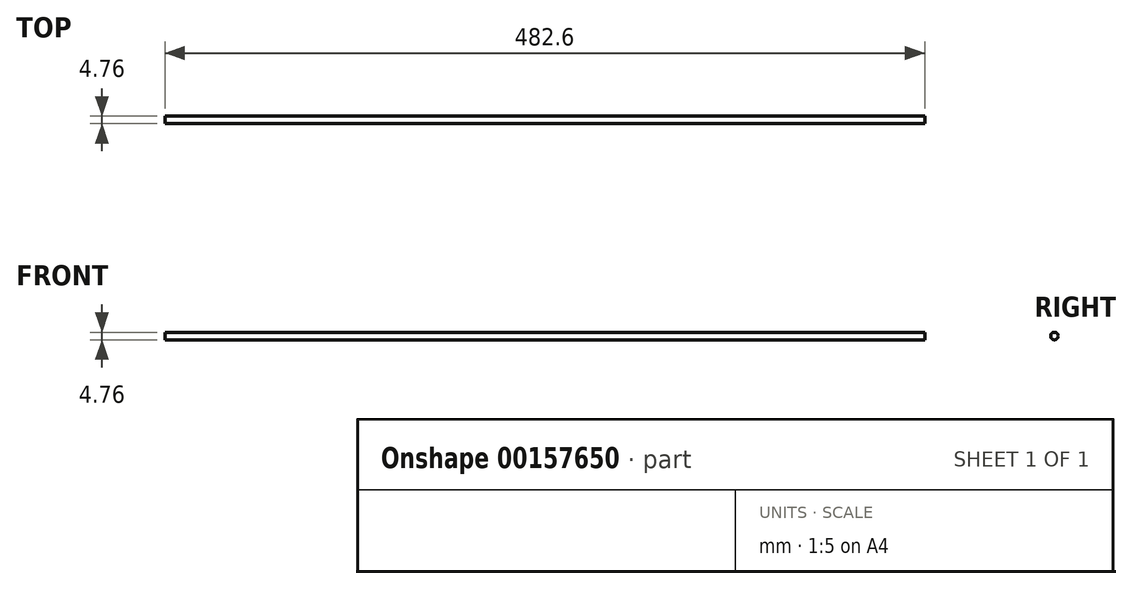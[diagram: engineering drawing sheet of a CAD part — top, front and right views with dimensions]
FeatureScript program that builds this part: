
annotation { "Feature Type Name" : "Feature", "Feature Type Description" : "" }
export const myFeature = defineFeature(function(context is Context, id is Id, definition is map)
    precondition{}
    {
        {
            var Q0;
            Q0=qCreatedBy(makeId("Right.planeOp"),FACE);
            var sketch = newSketch(context, id + "F0", { "sketchPlane" : qUnion([Q0])});
            skCircle(sketch, "E0", {"center": v(0, 0) * mm, "radius": 2.38 * mm});
            skSolve(sketch);
        }
        {
            var Q0;
            Q0=makeQuery(id+"F0.imprint","IMPRINT",FACE,{"disambiguationData":[TD([[makeQuery(id+"F0.imprint","IMPRINT",EDGE,{"derivedFrom":sQuery(id+"F0.wireOp",EDGE,"E0")}),1.0]])]});
            extrude(context, id + "F1", {"entities" : qUnion([Q0]), "oppositeDirection" : true, "depth" : 482.6 * mm});
        }
        {
            var Q0;
            Q0=qCreatedBy(makeId("Right.planeOp"),FACE);
            var sketch = newSketch(context, id + "F2", { "sketchPlane" : qUnion([Q0])});
            skCircle(sketch, "E1", {"center": v(-50.08, 0) * mm, "radius": 6.1 * mm});
            skCircle(sketch, "E2", {"center": v(-50.08, 0) * mm, "radius": 1.59 * mm});
            skSolve(sketch);
        }
        {
            var Q0;
            Q0=makeQuery(id+"F2.imprint","IMPRINT",FACE,{"disambiguationData":[TD([[makeQuery(id+"F2.imprint","IMPRINT",EDGE,{"derivedFrom":sQuery(id+"F2.wireOp",EDGE,"E1")}),1.0]])]});
            extrude(context, id + "F3", {"entities" : qUnion([Q0]), "oppositeDirection" : true, "depth" : 3.17 * mm});
        }
        {
            var Q0;
            Q0=makeQuery(id+"F3.opExtrude","SWEPT_BODY",BODY,{"disambiguationData":[OSD([sQuery(id+"F2.wireOp",EDGE,"E1"),sQuery(id+"F2.wireOp",EDGE,"E2")])]});
            deleteBodies(context, id + "F4", {"entities" : qUnion([Q0])});
        }
    });
